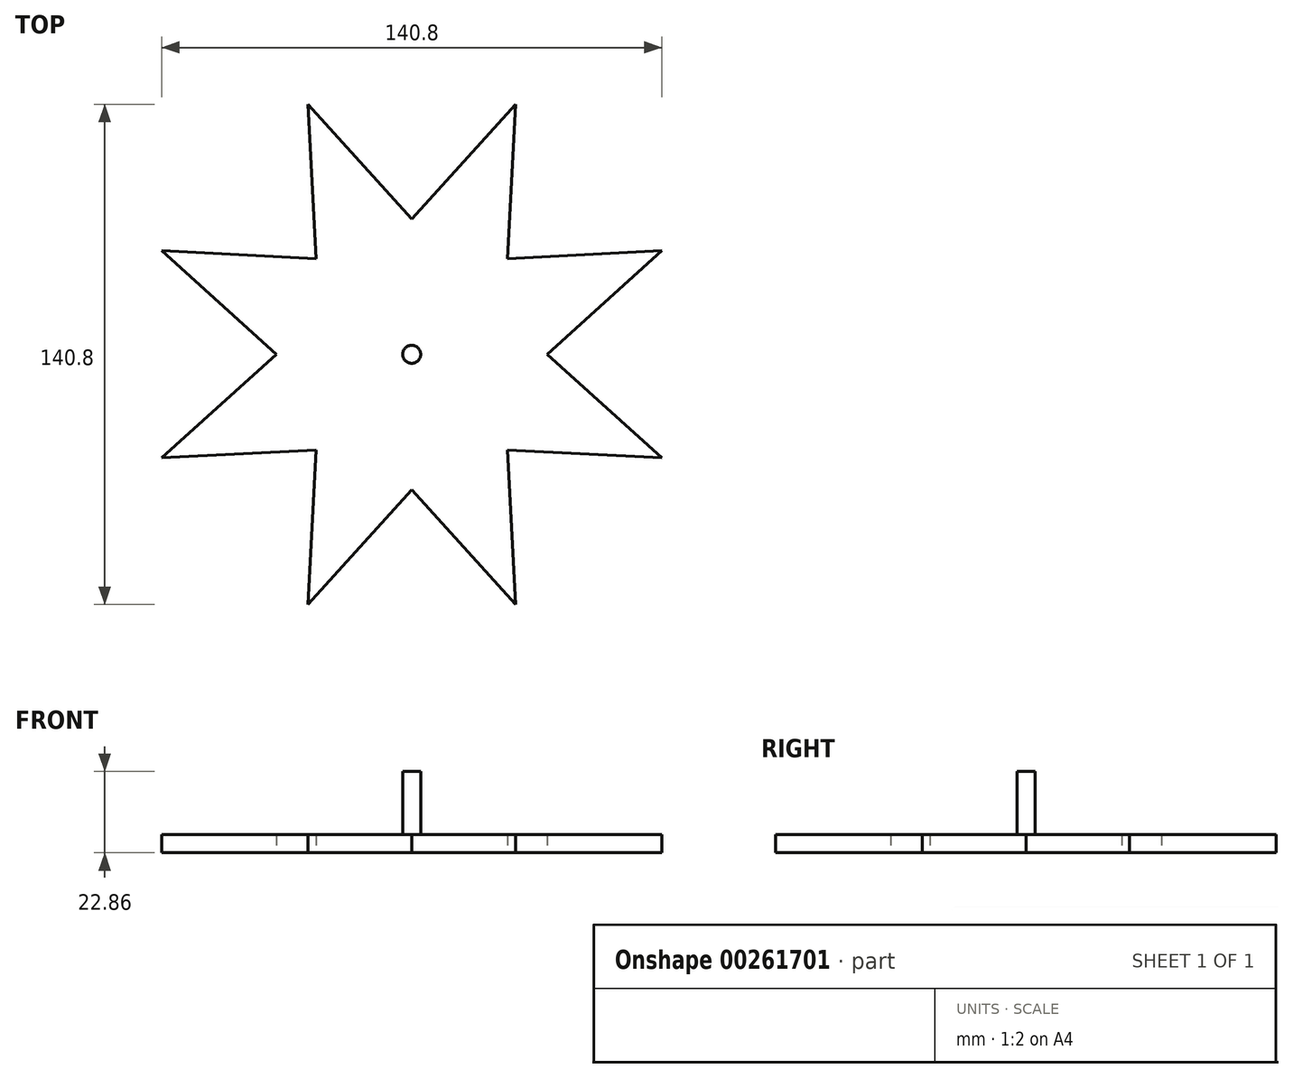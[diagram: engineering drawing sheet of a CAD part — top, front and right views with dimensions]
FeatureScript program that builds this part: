
annotation { "Feature Type Name" : "Feature", "Feature Type Description" : "" }
export const myFeature = defineFeature(function(context is Context, id is Id, definition is map)
    precondition{}
    {
        {
            var Q0;
            Q0=qCreatedBy(makeId("Top.planeOp"),FACE);
            var sketch = newSketch(context, id + "F0", { "sketchPlane" : qUnion([Q0])});
            skCircle(sketch, "E0", {"center": v(0, 0) * mm, "radius": 76.2 * mm});
            skCircle(sketch, "E1", {"center": v(0, 0) * mm, "radius": 38.1 * mm});
            skLineSegment(sketch, "E2", {"start": v(0, -76.2) * mm, "end": v(0, 76.2) * mm});
            skLineSegment(sketch, "E3", {"start": v(-76.2, 0) * mm, "end": v(76.2, 0) * mm});
            skLineSegment(sketch, "E4", {"start": v(53.88, -53.88) * mm, "end": v(-53.88, 53.88) * mm});
            skLineSegment(sketch, "E5", {"start": v(-53.88, -53.88) * mm, "end": v(53.88, 53.88) * mm});
            skLineSegment(sketch, "E6", {"start": v(-29.16, -70.4) * mm, "end": v(29.16, 70.4) * mm});
            skLineSegment(sketch, "E7", {"start": v(-29.16, 70.4) * mm, "end": v(29.16, -70.4) * mm});
            skLineSegment(sketch, "E8", {"start": v(-70.4, -29.16) * mm, "end": v(70.4, 29.16) * mm});
            skLineSegment(sketch, "E9", {"start": v(70.4, -29.16) * mm, "end": v(-70.4, 29.16) * mm});
            skCircle(sketch, "E10", {"center": v(0, 0) * mm, "radius": 2.54 * mm});
            skLineSegment(sketch, "E11", {"start": v(-29.16, 70.4) * mm, "end": v(0, 38.1) * mm});
            skLineSegment(sketch, "E12", {"start": v(0, 38.1) * mm, "end": v(29.16, 70.4) * mm});
            skLineSegment(sketch, "E13", {"start": v(29.16, 70.4) * mm, "end": v(26.94, 26.94) * mm});
            skLineSegment(sketch, "E14", {"start": v(26.94, 26.94) * mm, "end": v(70.4, 29.16) * mm});
            skLineSegment(sketch, "E15", {"start": v(70.4, 29.16) * mm, "end": v(38.1, 0) * mm});
            skLineSegment(sketch, "E16", {"start": v(38.1, 0) * mm, "end": v(70.4, -29.16) * mm});
            skLineSegment(sketch, "E17", {"start": v(70.4, -29.16) * mm, "end": v(26.94, -26.94) * mm});
            skLineSegment(sketch, "E18", {"start": v(26.94, -26.94) * mm, "end": v(29.16, -70.4) * mm});
            skLineSegment(sketch, "E19", {"start": v(29.16, -70.4) * mm, "end": v(0, -38.1) * mm});
            skLineSegment(sketch, "E20", {"start": v(0, -38.1) * mm, "end": v(-29.16, -70.4) * mm});
            skLineSegment(sketch, "E21", {"start": v(-29.16, -70.4) * mm, "end": v(-26.94, -26.94) * mm});
            skLineSegment(sketch, "E22", {"start": v(-26.94, -26.94) * mm, "end": v(-70.4, -29.16) * mm});
            skLineSegment(sketch, "E23", {"start": v(-70.4, -29.16) * mm, "end": v(-38.1, 0) * mm});
            skLineSegment(sketch, "E24", {"start": v(-38.1, 0) * mm, "end": v(-70.4, 29.16) * mm});
            skLineSegment(sketch, "E25", {"start": v(-70.4, 29.16) * mm, "end": v(-26.94, 26.94) * mm});
            skLineSegment(sketch, "E26", {"start": v(-26.94, 26.94) * mm, "end": v(-29.16, 70.4) * mm});
            skSolve(sketch);
        }
        {
            var Q0;
            {var subQ0=sQuery(id+"F0.wireOp",EDGE,"swhP0IIQ-2COe-3E9c-uLW2-dMsrqXERTyJQ");Q0=makeQuery(id+"F0.imprint","IMPRINT",FACE,{"disambiguationData":[TD([[makeQuery(id+"F0.imprint","IMPRINT",EDGE,{"derivedFrom":subQ0}),1.0]])]});}
            var Q1;
            {var subQ0=sQuery(id+"F0.wireOp",EDGE,"VLdgSWqC-VuDe-k1fp-PlBM-O2qoIRh2d9Fy");Q1=makeQuery(id+"F0.imprint","IMPRINT",FACE,{"disambiguationData":[TD([[makeQuery(id+"F0.imprint","IMPRINT",EDGE,{"derivedFrom":subQ0}),1.0]])]});}
            var Q2;
            {var subQ0=sQuery(id+"F0.wireOp",EDGE,"1Yreuqyj-sAfm-ohKM-625V-FKjGtg742c52");Q2=makeQuery(id+"F0.imprint","IMPRINT",FACE,{"disambiguationData":[TD([[makeQuery(id+"F0.imprint","IMPRINT",EDGE,{"derivedFrom":subQ0}),1.0]])]});}
            var Q3;
            {var subQ0=sQuery(id+"F0.wireOp",EDGE,"ecQaCsts-hoVW-mFr4-gLAy-7JOwEwJKK66O");Q3=makeQuery(id+"F0.imprint","IMPRINT",FACE,{"disambiguationData":[TD([[makeQuery(id+"F0.imprint","IMPRINT",EDGE,{"derivedFrom":subQ0}),1.0]])]});}
            var Q4;
            {var subQ0=sQuery(id+"F0.wireOp",EDGE,"v7lrhO8g-3sBl-4AiW-MCYy-V0c68UKBqu11");Q4=makeQuery(id+"F0.imprint","IMPRINT",FACE,{"disambiguationData":[TD([[makeQuery(id+"F0.imprint","IMPRINT",EDGE,{"derivedFrom":subQ0}),1.0]])]});}
            var Q5;
            {var subQ0=sQuery(id+"F0.wireOp",EDGE,"wsh1uI22-9fsO-KOZI-s8l2-L8XsledoB6xs");Q5=makeQuery(id+"F0.imprint","IMPRINT",FACE,{"disambiguationData":[TD([[makeQuery(id+"F0.imprint","IMPRINT",EDGE,{"derivedFrom":subQ0}),1.0]])]});}
            var Q6;
            {var subQ0=sQuery(id+"F0.wireOp",EDGE,"GY1RhF3Y-wne1-MJJU-AsoB-iguJOt9M9B1v");Q6=makeQuery(id+"F0.imprint","IMPRINT",FACE,{"disambiguationData":[TD([[makeQuery(id+"F0.imprint","IMPRINT",EDGE,{"derivedFrom":subQ0}),1.0]])]});}
            var Q7;
            {var subQ0=sQuery(id+"F0.wireOp",EDGE,"suNjp9kK-InvT-0bsU-0qs9-R4nzAMyA1MYn");Q7=makeQuery(id+"F0.imprint","IMPRINT",FACE,{"disambiguationData":[TD([[makeQuery(id+"F0.imprint","IMPRINT",EDGE,{"derivedFrom":subQ0}),1.0]])]});}
            var Q8;
            {var subQ0=sQuery(id+"F0.wireOp",EDGE,"L8RjwDeY-Veer-JCBu-UwXh-UQDld4SZEacD");Q8=makeQuery(id+"F0.imprint","IMPRINT",FACE,{"disambiguationData":[TD([[makeQuery(id+"F0.imprint","IMPRINT",EDGE,{"derivedFrom":subQ0}),1.0]])]});}
            var Q9;
            {var subQ0=sQuery(id+"F0.wireOp",EDGE,"vslZAwIb-nswC-95dR-FxVf-X9k6YOrbL659");Q9=makeQuery(id+"F0.imprint","IMPRINT",FACE,{"disambiguationData":[TD([[makeQuery(id+"F0.imprint","IMPRINT",EDGE,{"derivedFrom":subQ0}),1.0]])]});}
            var Q10;
            {var subQ0=sQuery(id+"F0.wireOp",EDGE,"0dtuZ5b5-ejoR-kj01-o66K-7Vu9oOP5AmB5");Q10=makeQuery(id+"F0.imprint","IMPRINT",FACE,{"disambiguationData":[TD([[makeQuery(id+"F0.imprint","IMPRINT",EDGE,{"derivedFrom":subQ0}),1.0]])]});}
            var Q11;
            {var subQ0=sQuery(id+"F0.wireOp",EDGE,"RVRRARdO-jyym-2Btk-sSIO-S7B2xUS1BkwM");Q11=makeQuery(id+"F0.imprint","IMPRINT",FACE,{"disambiguationData":[TD([[makeQuery(id+"F0.imprint","IMPRINT",EDGE,{"derivedFrom":subQ0}),1.0]])]});}
            var Q12;
            {var subQ0=sQuery(id+"F0.wireOp",EDGE,"ZpQ8Dqor-i8G8-2hwr-UcjQ-1G8HW7Qpk3Oo");Q12=makeQuery(id+"F0.imprint","IMPRINT",FACE,{"disambiguationData":[TD([[makeQuery(id+"F0.imprint","IMPRINT",EDGE,{"derivedFrom":subQ0}),1.0]])]});}
            var Q13;
            {var subQ0=sQuery(id+"F0.wireOp",EDGE,"ETO52JNF-6OdF-eQU2-V7bi-VHV1iqxInxch");Q13=makeQuery(id+"F0.imprint","IMPRINT",FACE,{"disambiguationData":[TD([[makeQuery(id+"F0.imprint","IMPRINT",EDGE,{"derivedFrom":subQ0}),1.0]])]});}
            var Q14;
            {var subQ0=sQuery(id+"F0.wireOp",EDGE,"BEa038G5-Rcns-34Qx-tPpq-rO0U58zGz1sa");Q14=makeQuery(id+"F0.imprint","IMPRINT",FACE,{"disambiguationData":[TD([[makeQuery(id+"F0.imprint","IMPRINT",EDGE,{"derivedFrom":subQ0}),1.0]])]});}
            var Q15;
            {var subQ0=sQuery(id+"F0.wireOp",EDGE,"7Agapx40-SDNZ-gmRW-8rdC-tYaPJHSMQIkg");Q15=makeQuery(id+"F0.imprint","IMPRINT",FACE,{"disambiguationData":[TD([[makeQuery(id+"F0.imprint","IMPRINT",EDGE,{"derivedFrom":subQ0}),1.0]])]});}
            var Q16;
            {var subQ0=sQuery(id+"F0.wireOp",EDGE,"E22");Q16=makeQuery(id+"F0.imprint","IMPRINT",FACE,{"disambiguationData":[TD([[makeQuery(id+"F0.imprint","IMPRINT",EDGE,{"derivedFrom":subQ0}),-1.0]])]});}
            var Q17;
            {var subQ0=sQuery(id+"F0.wireOp",EDGE,"E23");Q17=makeQuery(id+"F0.imprint","IMPRINT",FACE,{"disambiguationData":[TD([[makeQuery(id+"F0.imprint","IMPRINT",EDGE,{"derivedFrom":subQ0}),-1.0]])]});}
            var Q18;
            {var subQ0=sQuery(id+"F0.wireOp",EDGE,"E24");Q18=makeQuery(id+"F0.imprint","IMPRINT",FACE,{"disambiguationData":[TD([[makeQuery(id+"F0.imprint","IMPRINT",EDGE,{"derivedFrom":subQ0}),-1.0]])]});}
            var Q19;
            {var subQ0=sQuery(id+"F0.wireOp",EDGE,"E25");Q19=makeQuery(id+"F0.imprint","IMPRINT",FACE,{"disambiguationData":[TD([[makeQuery(id+"F0.imprint","IMPRINT",EDGE,{"derivedFrom":subQ0}),-1.0]])]});}
            var Q20;
            {var subQ0=sQuery(id+"F0.wireOp",EDGE,"E26");Q20=makeQuery(id+"F0.imprint","IMPRINT",FACE,{"disambiguationData":[TD([[makeQuery(id+"F0.imprint","IMPRINT",EDGE,{"derivedFrom":subQ0}),-1.0]])]});}
            var Q21;
            {var subQ0=sQuery(id+"F0.wireOp",EDGE,"E11");Q21=makeQuery(id+"F0.imprint","IMPRINT",FACE,{"disambiguationData":[TD([[makeQuery(id+"F0.imprint","IMPRINT",EDGE,{"derivedFrom":subQ0}),-1.0]])]});}
            var Q22;
            {var subQ0=sQuery(id+"F0.wireOp",EDGE,"E12");Q22=makeQuery(id+"F0.imprint","IMPRINT",FACE,{"disambiguationData":[TD([[makeQuery(id+"F0.imprint","IMPRINT",EDGE,{"derivedFrom":subQ0}),-1.0]])]});}
            var Q23;
            {var subQ0=sQuery(id+"F0.wireOp",EDGE,"E13");Q23=makeQuery(id+"F0.imprint","IMPRINT",FACE,{"disambiguationData":[TD([[makeQuery(id+"F0.imprint","IMPRINT",EDGE,{"derivedFrom":subQ0}),-1.0]])]});}
            var Q24;
            {var subQ0=sQuery(id+"F0.wireOp",EDGE,"E15");Q24=makeQuery(id+"F0.imprint","IMPRINT",FACE,{"disambiguationData":[TD([[makeQuery(id+"F0.imprint","IMPRINT",EDGE,{"derivedFrom":subQ0}),-1.0]])]});}
            var Q25;
            {var subQ0=sQuery(id+"F0.wireOp",EDGE,"E16");Q25=makeQuery(id+"F0.imprint","IMPRINT",FACE,{"disambiguationData":[TD([[makeQuery(id+"F0.imprint","IMPRINT",EDGE,{"derivedFrom":subQ0}),-1.0]])]});}
            var Q26;
            {var subQ0=sQuery(id+"F0.wireOp",EDGE,"E17");Q26=makeQuery(id+"F0.imprint","IMPRINT",FACE,{"disambiguationData":[TD([[makeQuery(id+"F0.imprint","IMPRINT",EDGE,{"derivedFrom":subQ0}),-1.0]])]});}
            var Q27;
            {var subQ0=sQuery(id+"F0.wireOp",EDGE,"E18");Q27=makeQuery(id+"F0.imprint","IMPRINT",FACE,{"disambiguationData":[TD([[makeQuery(id+"F0.imprint","IMPRINT",EDGE,{"derivedFrom":subQ0}),-1.0]])]});}
            var Q28;
            {var subQ0=sQuery(id+"F0.wireOp",EDGE,"E19");Q28=makeQuery(id+"F0.imprint","IMPRINT",FACE,{"disambiguationData":[TD([[makeQuery(id+"F0.imprint","IMPRINT",EDGE,{"derivedFrom":subQ0}),-1.0]])]});}
            var Q29;
            {var subQ0=sQuery(id+"F0.wireOp",EDGE,"E20");Q29=makeQuery(id+"F0.imprint","IMPRINT",FACE,{"disambiguationData":[TD([[makeQuery(id+"F0.imprint","IMPRINT",EDGE,{"derivedFrom":subQ0}),-1.0]])]});}
            var Q30;
            {var subQ0=sQuery(id+"F0.wireOp",EDGE,"E21");Q30=makeQuery(id+"F0.imprint","IMPRINT",FACE,{"disambiguationData":[TD([[makeQuery(id+"F0.imprint","IMPRINT",EDGE,{"derivedFrom":subQ0}),-1.0]])]});}
            var Q31;
            {var subQ1=sQuery(id+"F0.wireOp",EDGE,"E1");var subQ3=sQuery(id+"F0.wireOp",EDGE,"E6");var subQ4=makeQuery(id+"F0.imprint","INTERSECT",VERTEX,{"disambiguationData":[OD(1.0)],"derivedFrom":[subQ1,subQ3]});Q31=makeQuery(id+"F0.imprint","IMPRINT",FACE,{"disambiguationData":[TD([[makeQuery(id+"F0.imprint","IMPRINT",EDGE,{"disambiguationData":[TD([[subQ4,-1.0]])],"derivedFrom":subQ3}),1.0]])]});}
            var Q32;
            {var subQ1=sQuery(id+"F0.wireOp",EDGE,"E1");var subQ3=sQuery(id+"F0.wireOp",EDGE,"E6");var subQ4=makeQuery(id+"F0.imprint","INTERSECT",VERTEX,{"disambiguationData":[OD(1.0)],"derivedFrom":[subQ1,subQ3]});Q32=makeQuery(id+"F0.imprint","IMPRINT",FACE,{"disambiguationData":[TD([[makeQuery(id+"F0.imprint","IMPRINT",EDGE,{"disambiguationData":[TD([[subQ4,-1.0]])],"derivedFrom":subQ3}),-1.0]])]});}
            var Q33;
            {var subQ1=sQuery(id+"F0.wireOp",EDGE,"E1");var subQ3=sQuery(id+"F0.wireOp",EDGE,"E7");var subQ4=makeQuery(id+"F0.imprint","INTERSECT",VERTEX,{"disambiguationData":[OD(1.0)],"derivedFrom":[subQ1,subQ3]});Q33=makeQuery(id+"F0.imprint","IMPRINT",FACE,{"disambiguationData":[TD([[makeQuery(id+"F0.imprint","IMPRINT",EDGE,{"disambiguationData":[TD([[subQ4,1.0]])],"derivedFrom":subQ3}),-1.0]])]});}
            var Q34;
            {var subQ1=sQuery(id+"F0.wireOp",EDGE,"E1");var subQ3=sQuery(id+"F0.wireOp",EDGE,"E7");var subQ4=makeQuery(id+"F0.imprint","INTERSECT",VERTEX,{"disambiguationData":[OD(1.0)],"derivedFrom":[subQ1,subQ3]});Q34=makeQuery(id+"F0.imprint","IMPRINT",FACE,{"disambiguationData":[TD([[makeQuery(id+"F0.imprint","IMPRINT",EDGE,{"disambiguationData":[TD([[subQ4,1.0]])],"derivedFrom":subQ3}),1.0]])]});}
            var Q35;
            {var subQ1=sQuery(id+"F0.wireOp",EDGE,"E1");var subQ3=sQuery(id+"F0.wireOp",EDGE,"E9");var subQ4=makeQuery(id+"F0.imprint","INTERSECT",VERTEX,{"disambiguationData":[OD(1.0)],"derivedFrom":[subQ1,subQ3]});Q35=makeQuery(id+"F0.imprint","IMPRINT",FACE,{"disambiguationData":[TD([[makeQuery(id+"F0.imprint","IMPRINT",EDGE,{"disambiguationData":[TD([[subQ4,-1.0]])],"derivedFrom":subQ3}),1.0]])]});}
            var Q36;
            {var subQ1=sQuery(id+"F0.wireOp",EDGE,"E1");var subQ3=sQuery(id+"F0.wireOp",EDGE,"E9");var subQ4=makeQuery(id+"F0.imprint","INTERSECT",VERTEX,{"disambiguationData":[OD(1.0)],"derivedFrom":[subQ1,subQ3]});Q36=makeQuery(id+"F0.imprint","IMPRINT",FACE,{"disambiguationData":[TD([[makeQuery(id+"F0.imprint","IMPRINT",EDGE,{"disambiguationData":[TD([[subQ4,-1.0]])],"derivedFrom":subQ3}),-1.0]])]});}
            var Q37;
            {var subQ1=sQuery(id+"F0.wireOp",EDGE,"E1");var subQ3=sQuery(id+"F0.wireOp",EDGE,"E8");var subQ4=makeQuery(id+"F0.imprint","INTERSECT",VERTEX,{"disambiguationData":[OD(0.0)],"derivedFrom":[subQ1,subQ3]});Q37=makeQuery(id+"F0.imprint","IMPRINT",FACE,{"disambiguationData":[TD([[makeQuery(id+"F0.imprint","IMPRINT",EDGE,{"disambiguationData":[TD([[subQ4,1.0]])],"derivedFrom":subQ3}),-1.0]])]});}
            var Q38;
            {var subQ1=sQuery(id+"F0.wireOp",EDGE,"E1");var subQ3=sQuery(id+"F0.wireOp",EDGE,"E8");var subQ4=makeQuery(id+"F0.imprint","INTERSECT",VERTEX,{"disambiguationData":[OD(0.0)],"derivedFrom":[subQ1,subQ3]});Q38=makeQuery(id+"F0.imprint","IMPRINT",FACE,{"disambiguationData":[TD([[makeQuery(id+"F0.imprint","IMPRINT",EDGE,{"disambiguationData":[TD([[subQ4,1.0]])],"derivedFrom":subQ3}),1.0]])]});}
            var Q39;
            {var subQ1=sQuery(id+"F0.wireOp",EDGE,"E1");var subQ3=sQuery(id+"F0.wireOp",EDGE,"E6");var subQ4=makeQuery(id+"F0.imprint","INTERSECT",VERTEX,{"disambiguationData":[OD(0.0)],"derivedFrom":[subQ1,subQ3]});Q39=makeQuery(id+"F0.imprint","IMPRINT",FACE,{"disambiguationData":[TD([[makeQuery(id+"F0.imprint","IMPRINT",EDGE,{"disambiguationData":[TD([[subQ4,1.0]])],"derivedFrom":subQ3}),-1.0]])]});}
            var Q40;
            {var subQ1=sQuery(id+"F0.wireOp",EDGE,"E1");var subQ3=sQuery(id+"F0.wireOp",EDGE,"E6");var subQ4=makeQuery(id+"F0.imprint","INTERSECT",VERTEX,{"disambiguationData":[OD(0.0)],"derivedFrom":[subQ1,subQ3]});Q40=makeQuery(id+"F0.imprint","IMPRINT",FACE,{"disambiguationData":[TD([[makeQuery(id+"F0.imprint","IMPRINT",EDGE,{"disambiguationData":[TD([[subQ4,1.0]])],"derivedFrom":subQ3}),1.0]])]});}
            var Q41;
            {var subQ1=sQuery(id+"F0.wireOp",EDGE,"E1");var subQ3=sQuery(id+"F0.wireOp",EDGE,"E7");var subQ4=makeQuery(id+"F0.imprint","INTERSECT",VERTEX,{"disambiguationData":[OD(0.0)],"derivedFrom":[subQ1,subQ3]});Q41=makeQuery(id+"F0.imprint","IMPRINT",FACE,{"disambiguationData":[TD([[makeQuery(id+"F0.imprint","IMPRINT",EDGE,{"disambiguationData":[TD([[subQ4,-1.0]])],"derivedFrom":subQ3}),1.0]])]});}
            var Q42;
            {var subQ1=sQuery(id+"F0.wireOp",EDGE,"E1");var subQ3=sQuery(id+"F0.wireOp",EDGE,"E7");var subQ4=makeQuery(id+"F0.imprint","INTERSECT",VERTEX,{"disambiguationData":[OD(0.0)],"derivedFrom":[subQ1,subQ3]});Q42=makeQuery(id+"F0.imprint","IMPRINT",FACE,{"disambiguationData":[TD([[makeQuery(id+"F0.imprint","IMPRINT",EDGE,{"disambiguationData":[TD([[subQ4,-1.0]])],"derivedFrom":subQ3}),-1.0]])]});}
            var Q43;
            {var subQ1=sQuery(id+"F0.wireOp",EDGE,"E1");var subQ3=sQuery(id+"F0.wireOp",EDGE,"E9");var subQ4=makeQuery(id+"F0.imprint","INTERSECT",VERTEX,{"disambiguationData":[OD(0.0)],"derivedFrom":[subQ1,subQ3]});Q43=makeQuery(id+"F0.imprint","IMPRINT",FACE,{"disambiguationData":[TD([[makeQuery(id+"F0.imprint","IMPRINT",EDGE,{"disambiguationData":[TD([[subQ4,1.0]])],"derivedFrom":subQ3}),-1.0]])]});}
            var Q44;
            {var subQ1=sQuery(id+"F0.wireOp",EDGE,"E1");var subQ3=sQuery(id+"F0.wireOp",EDGE,"E9");var subQ4=makeQuery(id+"F0.imprint","INTERSECT",VERTEX,{"disambiguationData":[OD(0.0)],"derivedFrom":[subQ1,subQ3]});Q44=makeQuery(id+"F0.imprint","IMPRINT",FACE,{"disambiguationData":[TD([[makeQuery(id+"F0.imprint","IMPRINT",EDGE,{"disambiguationData":[TD([[subQ4,1.0]])],"derivedFrom":subQ3}),1.0]])]});}
            var Q45;
            {var subQ1=sQuery(id+"F0.wireOp",EDGE,"E1");var subQ3=sQuery(id+"F0.wireOp",EDGE,"E8");var subQ4=makeQuery(id+"F0.imprint","INTERSECT",VERTEX,{"disambiguationData":[OD(1.0)],"derivedFrom":[subQ1,subQ3]});Q45=makeQuery(id+"F0.imprint","IMPRINT",FACE,{"disambiguationData":[TD([[makeQuery(id+"F0.imprint","IMPRINT",EDGE,{"disambiguationData":[TD([[subQ4,-1.0]])],"derivedFrom":subQ3}),1.0]])]});}
            var Q46;
            {var subQ1=sQuery(id+"F0.wireOp",EDGE,"E1");var subQ3=sQuery(id+"F0.wireOp",EDGE,"E8");var subQ4=makeQuery(id+"F0.imprint","INTERSECT",VERTEX,{"disambiguationData":[OD(1.0)],"derivedFrom":[subQ1,subQ3]});Q46=makeQuery(id+"F0.imprint","IMPRINT",FACE,{"disambiguationData":[TD([[makeQuery(id+"F0.imprint","IMPRINT",EDGE,{"disambiguationData":[TD([[subQ4,-1.0]])],"derivedFrom":subQ3}),-1.0]])]});}
            var Q47;
            {var subQ0=sQuery(id+"F0.wireOp",EDGE,"E14");Q47=makeQuery(id+"F0.imprint","IMPRINT",FACE,{"disambiguationData":[TD([[makeQuery(id+"F0.imprint","IMPRINT",EDGE,{"derivedFrom":subQ0}),-1.0]])]});}
            extrude(context, id + "F1", {"entities" : qUnion([Q0, Q1, Q2, Q3, Q4, Q5, Q6, Q7, Q8, Q9, Q10, Q11, Q12, Q13, Q14, Q15, Q16, Q17, Q18, Q19, Q20, Q21, Q22, Q23, Q24, Q25, Q26, Q27, Q28, Q29, Q30, Q31, Q32, Q33, Q34, Q35, Q36, Q37, Q38, Q39, Q40, Q41, Q42, Q43, Q44, Q45, Q46, Q47]), "depth" : 5.08 * mm});
        }
        {
            var Q0;
            {var subQ0=sQuery(id+"F0.wireOp",EDGE,"E10");var subQ1=sQuery(id+"F0.wireOp",EDGE,"E4");var subQ2=makeQuery(id+"F0.imprint","INTERSECT",VERTEX,{"disambiguationData":[OD(1.0)],"derivedFrom":[subQ1,subQ0]});Q0=makeQuery(id+"F0.imprint","IMPRINT",FACE,{"disambiguationData":[TD([[makeQuery(id+"F0.imprint","IMPRINT",EDGE,{"disambiguationData":[TD([[subQ2,1.0]])],"derivedFrom":subQ0}),1.0]])]});}
            var Q1;
            {var subQ0=sQuery(id+"F0.wireOp",EDGE,"E10");var subQ1=sQuery(id+"F0.wireOp",EDGE,"E4");var subQ2=makeQuery(id+"F0.imprint","INTERSECT",VERTEX,{"disambiguationData":[OD(1.0)],"derivedFrom":[subQ1,subQ0]});Q1=makeQuery(id+"F0.imprint","IMPRINT",FACE,{"disambiguationData":[TD([[makeQuery(id+"F0.imprint","IMPRINT",EDGE,{"disambiguationData":[TD([[subQ2,-1.0]])],"derivedFrom":subQ0}),1.0]])]});}
            var Q2;
            {var subQ0=sQuery(id+"F0.wireOp",EDGE,"E10");var subQ1=sQuery(id+"F0.wireOp",EDGE,"E3");var subQ2=makeQuery(id+"F0.imprint","INTERSECT",VERTEX,{"disambiguationData":[OD(0.0)],"derivedFrom":[subQ1,subQ0]});Q2=makeQuery(id+"F0.imprint","IMPRINT",FACE,{"disambiguationData":[TD([[makeQuery(id+"F0.imprint","IMPRINT",EDGE,{"disambiguationData":[TD([[subQ2,1.0]])],"derivedFrom":subQ0}),1.0]])]});}
            var Q3;
            {var subQ0=sQuery(id+"F0.wireOp",EDGE,"E10");var subQ1=sQuery(id+"F0.wireOp",EDGE,"E3");var subQ2=makeQuery(id+"F0.imprint","INTERSECT",VERTEX,{"disambiguationData":[OD(0.0)],"derivedFrom":[subQ1,subQ0]});Q3=makeQuery(id+"F0.imprint","IMPRINT",FACE,{"disambiguationData":[TD([[makeQuery(id+"F0.imprint","IMPRINT",EDGE,{"disambiguationData":[TD([[subQ2,-1.0]])],"derivedFrom":subQ0}),1.0]])]});}
            var Q4;
            {var subQ0=sQuery(id+"F0.wireOp",EDGE,"E10");var subQ1=sQuery(id+"F0.wireOp",EDGE,"E5");var subQ2=makeQuery(id+"F0.imprint","INTERSECT",VERTEX,{"disambiguationData":[OD(0.0)],"derivedFrom":[subQ1,subQ0]});Q4=makeQuery(id+"F0.imprint","IMPRINT",FACE,{"disambiguationData":[TD([[makeQuery(id+"F0.imprint","IMPRINT",EDGE,{"disambiguationData":[TD([[subQ2,1.0]])],"derivedFrom":subQ0}),1.0]])]});}
            var Q5;
            {var subQ0=sQuery(id+"F0.wireOp",EDGE,"E10");var subQ1=sQuery(id+"F0.wireOp",EDGE,"E5");var subQ2=makeQuery(id+"F0.imprint","INTERSECT",VERTEX,{"disambiguationData":[OD(0.0)],"derivedFrom":[subQ1,subQ0]});Q5=makeQuery(id+"F0.imprint","IMPRINT",FACE,{"disambiguationData":[TD([[makeQuery(id+"F0.imprint","IMPRINT",EDGE,{"disambiguationData":[TD([[subQ2,-1.0]])],"derivedFrom":subQ0}),1.0]])]});}
            var Q6;
            {var subQ0=sQuery(id+"F0.wireOp",EDGE,"E10");var subQ1=sQuery(id+"F0.wireOp",EDGE,"E2");var subQ2=makeQuery(id+"F0.imprint","INTERSECT",VERTEX,{"disambiguationData":[OD(0.0)],"derivedFrom":[subQ1,subQ0]});Q6=makeQuery(id+"F0.imprint","IMPRINT",FACE,{"disambiguationData":[TD([[makeQuery(id+"F0.imprint","IMPRINT",EDGE,{"disambiguationData":[TD([[subQ2,1.0]])],"derivedFrom":subQ0}),1.0]])]});}
            var Q7;
            {var subQ0=sQuery(id+"F0.wireOp",EDGE,"E10");var subQ1=sQuery(id+"F0.wireOp",EDGE,"E2");var subQ2=makeQuery(id+"F0.imprint","INTERSECT",VERTEX,{"disambiguationData":[OD(0.0)],"derivedFrom":[subQ1,subQ0]});Q7=makeQuery(id+"F0.imprint","IMPRINT",FACE,{"disambiguationData":[TD([[makeQuery(id+"F0.imprint","IMPRINT",EDGE,{"disambiguationData":[TD([[subQ2,-1.0]])],"derivedFrom":subQ0}),1.0]])]});}
            var Q8;
            {var subQ0=sQuery(id+"F0.wireOp",EDGE,"E10");var subQ1=sQuery(id+"F0.wireOp",EDGE,"E4");var subQ2=makeQuery(id+"F0.imprint","INTERSECT",VERTEX,{"disambiguationData":[OD(0.0)],"derivedFrom":[subQ1,subQ0]});Q8=makeQuery(id+"F0.imprint","IMPRINT",FACE,{"disambiguationData":[TD([[makeQuery(id+"F0.imprint","IMPRINT",EDGE,{"disambiguationData":[TD([[subQ2,1.0]])],"derivedFrom":subQ0}),1.0]])]});}
            var Q9;
            {var subQ0=sQuery(id+"F0.wireOp",EDGE,"E10");var subQ1=sQuery(id+"F0.wireOp",EDGE,"E4");var subQ2=makeQuery(id+"F0.imprint","INTERSECT",VERTEX,{"disambiguationData":[OD(0.0)],"derivedFrom":[subQ1,subQ0]});Q9=makeQuery(id+"F0.imprint","IMPRINT",FACE,{"disambiguationData":[TD([[makeQuery(id+"F0.imprint","IMPRINT",EDGE,{"disambiguationData":[TD([[subQ2,-1.0]])],"derivedFrom":subQ0}),1.0]])]});}
            var Q10;
            {var subQ0=sQuery(id+"F0.wireOp",EDGE,"E10");var subQ1=sQuery(id+"F0.wireOp",EDGE,"E3");var subQ2=makeQuery(id+"F0.imprint","INTERSECT",VERTEX,{"disambiguationData":[OD(1.0)],"derivedFrom":[subQ1,subQ0]});Q10=makeQuery(id+"F0.imprint","IMPRINT",FACE,{"disambiguationData":[TD([[makeQuery(id+"F0.imprint","IMPRINT",EDGE,{"disambiguationData":[TD([[subQ2,1.0]])],"derivedFrom":subQ0}),1.0]])]});}
            var Q11;
            {var subQ0=sQuery(id+"F0.wireOp",EDGE,"E10");var subQ1=sQuery(id+"F0.wireOp",EDGE,"E3");var subQ2=makeQuery(id+"F0.imprint","INTERSECT",VERTEX,{"disambiguationData":[OD(1.0)],"derivedFrom":[subQ1,subQ0]});Q11=makeQuery(id+"F0.imprint","IMPRINT",FACE,{"disambiguationData":[TD([[makeQuery(id+"F0.imprint","IMPRINT",EDGE,{"disambiguationData":[TD([[subQ2,-1.0]])],"derivedFrom":subQ0}),1.0]])]});}
            var Q12;
            {var subQ0=sQuery(id+"F0.wireOp",EDGE,"E10");var subQ1=sQuery(id+"F0.wireOp",EDGE,"E5");var subQ2=makeQuery(id+"F0.imprint","INTERSECT",VERTEX,{"disambiguationData":[OD(1.0)],"derivedFrom":[subQ1,subQ0]});Q12=makeQuery(id+"F0.imprint","IMPRINT",FACE,{"disambiguationData":[TD([[makeQuery(id+"F0.imprint","IMPRINT",EDGE,{"disambiguationData":[TD([[subQ2,1.0]])],"derivedFrom":subQ0}),1.0]])]});}
            var Q13;
            {var subQ0=sQuery(id+"F0.wireOp",EDGE,"E10");var subQ1=sQuery(id+"F0.wireOp",EDGE,"E2");var subQ2=makeQuery(id+"F0.imprint","INTERSECT",VERTEX,{"disambiguationData":[OD(1.0)],"derivedFrom":[subQ1,subQ0]});Q13=makeQuery(id+"F0.imprint","IMPRINT",FACE,{"disambiguationData":[TD([[makeQuery(id+"F0.imprint","IMPRINT",EDGE,{"disambiguationData":[TD([[subQ2,1.0]])],"derivedFrom":subQ0}),1.0]])]});}
            var Q14;
            {var subQ0=sQuery(id+"F0.wireOp",EDGE,"E10");var subQ1=sQuery(id+"F0.wireOp",EDGE,"E2");var subQ2=makeQuery(id+"F0.imprint","INTERSECT",VERTEX,{"disambiguationData":[OD(1.0)],"derivedFrom":[subQ1,subQ0]});Q14=makeQuery(id+"F0.imprint","IMPRINT",FACE,{"disambiguationData":[TD([[makeQuery(id+"F0.imprint","IMPRINT",EDGE,{"disambiguationData":[TD([[subQ2,-1.0]])],"derivedFrom":subQ0}),1.0]])]});}
            var Q15;
            {var subQ0=sQuery(id+"F0.wireOp",EDGE,"E10");var subQ1=sQuery(id+"F0.wireOp",EDGE,"E5");var subQ2=makeQuery(id+"F0.imprint","INTERSECT",VERTEX,{"disambiguationData":[OD(1.0)],"derivedFrom":[subQ1,subQ0]});Q15=makeQuery(id+"F0.imprint","IMPRINT",FACE,{"disambiguationData":[TD([[makeQuery(id+"F0.imprint","IMPRINT",EDGE,{"disambiguationData":[TD([[subQ2,-1.0]])],"derivedFrom":subQ0}),1.0]])]});}
            extrude(context, id + "F2", {"entities" : qUnion([Q0, Q1, Q2, Q3, Q4, Q5, Q6, Q7, Q8, Q9, Q10, Q11, Q12, Q13, Q14, Q15]), "operationType" : NewBodyOperationType.ADD, "depth" : 22.86 * mm});
        }
    });
